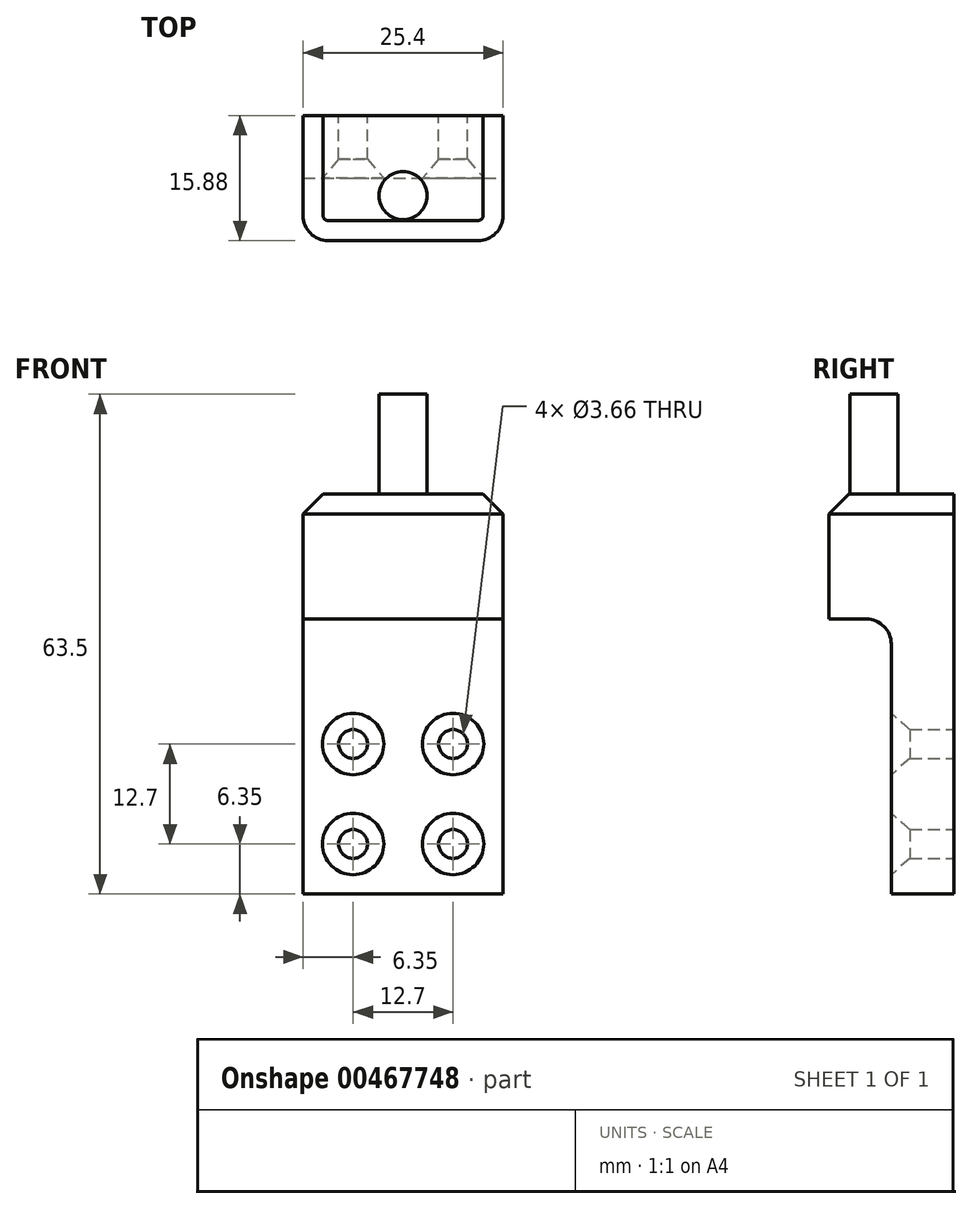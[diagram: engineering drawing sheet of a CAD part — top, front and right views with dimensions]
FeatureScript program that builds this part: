
annotation { "Feature Type Name" : "Feature", "Feature Type Description" : "" }
export const myFeature = defineFeature(function(context is Context, id is Id, definition is map)
    precondition{}
    {
        {
            var Q0;
            Q0=qCreatedBy(makeId("Front.planeOp"),FACE);
            var sketch = newSketch(context, id + "F0", { "sketchPlane" : qUnion([Q0])});
            skLineSegment(sketch, "E0.bottom", {"start": v(-12.7, 0) * mm, "end": v(12.7, 0) * mm});
            skLineSegment(sketch, "E0.top", {"start": v(-12.7, -50.8) * mm, "end": v(12.7, -50.8) * mm});
            skLineSegment(sketch, "E0.left", {"start": v(-12.7, 0) * mm, "end": v(-12.7, -50.8) * mm});
            skLineSegment(sketch, "E0.right", {"start": v(12.7, 0) * mm, "end": v(12.7, -50.8) * mm});
            skLineSegment(sketch, "E1", {"start": v(0, 33.68) * mm, "end": v(0, -101.13) * mm, "construction": true});
            skSolve(sketch);
        }
        {
            var Q0;
            Q0 = qSketchRegion(id + "F0", true);
            extrude(context, id + "F1", {"entities" : qUnion([Q0]), "depth" : 15.88 * mm});
        }
        {
            var Q0;
            Q0=makeQuery(id+"F1.opExtrude","SWEPT_FACE",FACE,{"disambiguationData":[OSD([sQuery(id+"F0.wireOp",EDGE,"E0.bottom")])]});
            var sketch = newSketch(context, id + "F2", { "sketchPlane" : qUnion([Q0])});
            skCircle(sketch, "E2", {"center": v(0, -10.16) * mm, "radius": 3.05 * mm});
            skPoint(sketch, "E2.centerSnap0", {"position": v(0, -15.88) * mm});
            skSolve(sketch);
        }
        {
            var Q0;
            Q0=makeQuery(id+"F2.imprint","IMPRINT",FACE,{"disambiguationData":[TD([[makeQuery(id+"F2.imprint","IMPRINT",EDGE,{"derivedFrom":sQuery(id+"F2.wireOp",EDGE,"E2")}),1.0]])]});
            extrude(context, id + "F3", {"entities" : qUnion([Q0]), "operationType" : NewBodyOperationType.ADD, "depth" : 12.7 * mm});
        }
        {
            var Q0;
            Q0=makeQuery(id+"F1.opExtrude","SWEPT_FACE",FACE,{"disambiguationData":[OSD([sQuery(id+"F0.wireOp",EDGE,"E0.right")])]});
            var sketch = newSketch(context, id + "F4", { "sketchPlane" : qUnion([Q0])});
            skLineSegment(sketch, "E3.bottom", {"start": v(-15.88, -50.8) * mm, "end": v(-7.94, -50.8) * mm});
            skLineSegment(sketch, "E3.top", {"start": v(-15.88, -15.88) * mm, "end": v(-7.94, -15.87) * mm});
            skLineSegment(sketch, "E3.left", {"start": v(-15.88, -50.8) * mm, "end": v(-15.88, -15.88) * mm});
            skLineSegment(sketch, "E3.right", {"start": v(-7.94, -50.8) * mm, "end": v(-7.94, -15.87) * mm});
            skSolve(sketch);
        }
        {
            var Q0;
            Q0=makeQuery(id+"F4.imprint","IMPRINT",FACE,{"disambiguationData":[TD([[makeQuery(id+"F4.imprint","IMPRINT",EDGE,{"derivedFrom":sQuery(id+"F4.wireOp",EDGE,"E3.bottom")}),1.0]])]});
            extrude(context, id + "F5", {"entities" : qUnion([Q0]), "operationType" : NewBodyOperationType.REMOVE, "endBound" : BoundingType.UP_TO_NEXT, "oppositeDirection" : true, "depth" : 25.4 * mm});
        }
        {
            var Q0;
            Q0=makeQuery(id+"F1.opExtrude","CAP_EDGE",EDGE,{"disambiguationData":[OSD([sQuery(id+"F0.wireOp",EDGE,"E0.right")])],"isStart":false});
            var Q1;
            Q1=makeQuery(id+"F1.opExtrude","CAP_EDGE",EDGE,{"disambiguationData":[OSD([sQuery(id+"F0.wireOp",EDGE,"E0.left")])],"isStart":false});
            var Q2;
            Q2=makeQuery(id+"F5.boolean.opBoolean","COPY",EDGE,{"derivedFrom":makeQuery(id+"F5.opExtrude","SWEPT_EDGE",EDGE,{"disambiguationData":[OSD([sQuery(id+"F4.wireOp",EDGE,"E3.top"),sQuery(id+"F4.wireOp",EDGE,"E3.right")])]})});
            fillet(context, id + "F6", {"entities" : qUnion([Q0, Q1, Q2]), "radius" : 3.17 * mm, "tangentPropagation" : true, "allowEdgeOverflow" : false});
        }
        {
            var Q0;
            Q0=makeQuery(id+"F5.boolean.opBoolean","COPY",FACE,{"derivedFrom":makeQuery(id+"F5.opExtrude","SWEPT_FACE",FACE,{"disambiguationData":[OSD([sQuery(id+"F4.wireOp",EDGE,"E3.right")])]})});
            var sketch = newSketch(context, id + "F7", { "sketchPlane" : qUnion([Q0])});
            skLineSegment(sketch, "E4.bottom", {"start": v(-6.35, -31.75) * mm, "end": v(6.35, -31.75) * mm, "construction": true});
            skLineSegment(sketch, "E4.top", {"start": v(-6.35, -44.45) * mm, "end": v(6.35, -44.45) * mm, "construction": true});
            skLineSegment(sketch, "E4.left", {"start": v(-6.35, -31.75) * mm, "end": v(-6.35, -44.45) * mm, "construction": true});
            skLineSegment(sketch, "E4.right", {"start": v(6.35, -31.75) * mm, "end": v(6.35, -44.45) * mm, "construction": true});
            skPoint(sketch, "E5", {"position": v(-6.35, -31.75) * mm});
            skPoint(sketch, "E6", {"position": v(6.35, -31.75) * mm});
            skPoint(sketch, "E7", {"position": v(6.35, -44.45) * mm});
            skPoint(sketch, "E8", {"position": v(-6.35, -44.45) * mm});
            skSolve(sketch);
        }
        {
            var Q0;
            Q0=sQuery(id+"F7.wireOp",VERTEX,"E5");
            var Q1;
            Q1=sQuery(id+"F7.wireOp",VERTEX,"E6");
            var Q2;
            Q2=sQuery(id+"F7.wireOp",VERTEX,"E7");
            var Q3;
            Q3=sQuery(id+"F7.wireOp",VERTEX,"E8");
            var Q4;
            Q4=makeQuery(id+"F1.opExtrude","SWEPT_BODY",BODY,{"disambiguationData":[OSD([sQuery(id+"F0.wireOp",EDGE,"E0.bottom"),sQuery(id+"F0.wireOp",EDGE,"E0.top"),sQuery(id+"F0.wireOp",EDGE,"E0.left"),sQuery(id+"F0.wireOp",EDGE,"E0.right")])]});
            hole(context, id + "F8", {"style" : HoleStyle.C_SINK, "endStyle" : HoleEndStyle.THROUGH, "standardTappedOrClearance" : lookupTablePath({ "standard" : "ANSI", "fit" : "Close", "size" : "#6", "type" : "Clearance" }), "standardBlindInLast" : lookupTablePath({ "fit" : "Close", "standard" : "ANSI", "size" : "#6", "type" : "Clearance" }), "holeDiameter" : 3.66 * mm, "cSinkDiameter" : 7.8 * mm, "cSinkAngle" : 82 * degree, "tappedDepth" : 12.7 * mm, "tapClearance" : 3, "locations" : qUnion([Q0, Q1, Q2, Q3]), "scope" : qUnion([Q4]), "startStyle" : HoleStartStyle.SKETCH});
        }
        {
            var Q0;
            Q0=makeQuery(id+"F1.opExtrude","CAP_EDGE",EDGE,{"disambiguationData":[OSD([sQuery(id+"F0.wireOp",EDGE,"E0.bottom")])],"isStart":false});
            chamfer(context, id + "F9", {"entities" : qUnion([Q0]), "width" : 2.54 * mm, "tangentPropagation" : true});
        }
    });
